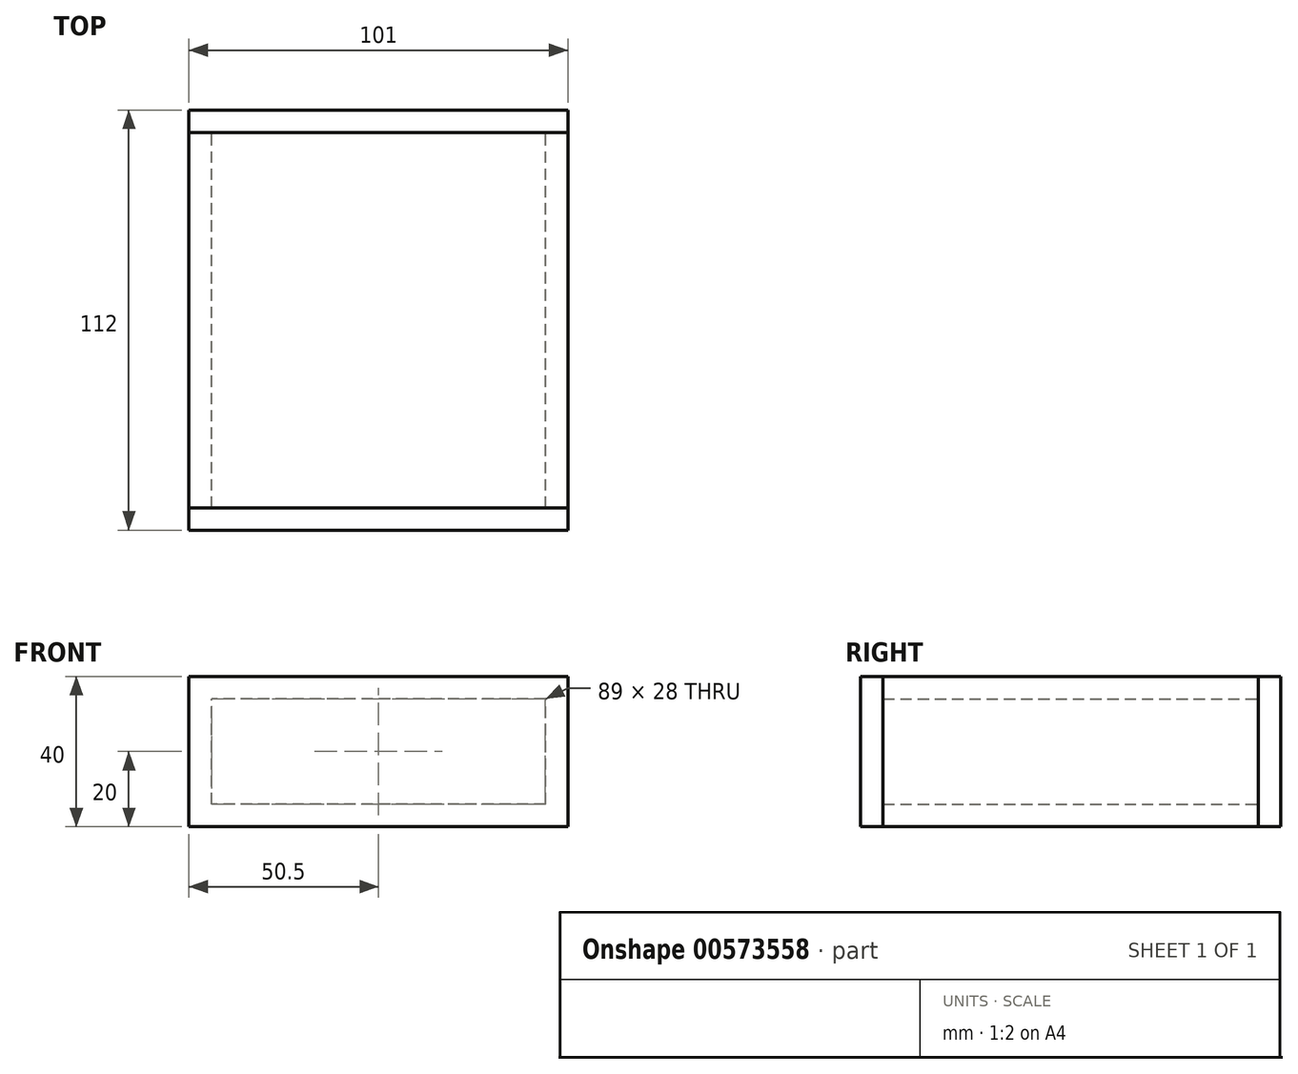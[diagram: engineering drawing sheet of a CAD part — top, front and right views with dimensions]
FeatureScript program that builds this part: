
annotation { "Feature Type Name" : "Feature", "Feature Type Description" : "" }
export const myFeature = defineFeature(function(context is Context, id is Id, definition is map)
    precondition{}
    {
        {
            var Q0;
            Q0=qCreatedBy(makeId("Front.planeOp"),FACE);
            var sketch = newSketch(context, id + "F0", { "sketchPlane" : qUnion([Q0])});
            skLineSegment(sketch, "E0.bottom", {"start": v(50.5, -20) * mm, "end": v(-50.5, -20) * mm});
            skLineSegment(sketch, "E0.top", {"start": v(50.5, 20) * mm, "end": v(-50.5, 20) * mm});
            skLineSegment(sketch, "E0.left", {"start": v(50.5, -20) * mm, "end": v(50.5, 20) * mm});
            skLineSegment(sketch, "E0.right", {"start": v(-50.5, -20) * mm, "end": v(-50.5, 20) * mm});
            skPoint(sketch, "E0.middle", {"position": v(0, 0) * mm});
            skSolve(sketch);
        }
        {
            var Q0;
            Q0=makeQuery(id+"F0.imprint","IMPRINT",FACE,{"disambiguationData":[TD([[makeQuery(id+"F0.imprint","IMPRINT",EDGE,{"derivedFrom":sQuery(id+"F0.wireOp",EDGE,"E0.bottom")}),-1.0]])]});
            extrude(context, id + "F1", {"entities" : qUnion([Q0]), "depth" : 6 * mm, "offsetDistance" : 25 * mm});
        }
        {
            var Q0;
            Q0=makeQuery(id+"F1.opExtrude","CAP_FACE",FACE,{"disambiguationData":[OSD([sQuery(id+"F0.wireOp",EDGE,"E0.bottom"),sQuery(id+"F0.wireOp",EDGE,"E0.top"),sQuery(id+"F0.wireOp",EDGE,"E0.left"),sQuery(id+"F0.wireOp",EDGE,"E0.right")])],"isStart":false});
            var sketch = newSketch(context, id + "F2", { "sketchPlane" : qUnion([Q0])});
            skLineSegment(sketch, "E1.0", {"start": v(50.5, -20) * mm, "end": v(50.5, 20) * mm});
            skLineSegment(sketch, "E2.0", {"start": v(50.5, 20) * mm, "end": v(-50.5, 20) * mm});
            skLineSegment(sketch, "E3.0", {"start": v(50.5, -20) * mm, "end": v(-50.5, -20) * mm});
            skLineSegment(sketch, "E4.0", {"start": v(-50.5, -20) * mm, "end": v(-50.5, 20) * mm});
            skLineSegment(sketch, "E5.0", {"start": v(44.5, -14) * mm, "end": v(44.5, 14) * mm});
            skLineSegment(sketch, "E5.1", {"start": v(44.5, -14) * mm, "end": v(-44.5, -14) * mm});
            skLineSegment(sketch, "E5.2", {"start": v(-44.5, -14) * mm, "end": v(-44.5, 14) * mm});
            skLineSegment(sketch, "E5.3", {"start": v(44.5, 14) * mm, "end": v(-44.5, 14) * mm});
            skSolve(sketch);
        }
        {
            var Q0;
            Q0 = qSketchRegion(id + "F2", true);
            extrude(context, id + "F3", {"entities" : qUnion([Q0]), "depth" : 100 * mm, "offsetDistance" : 25 * mm});
        }
        {
            var Q0;
            Q0=makeQuery(id+"F1.opExtrude","SWEPT_BODY",BODY,{"disambiguationData":[OSD([sQuery(id+"F0.wireOp",EDGE,"E0.bottom"),sQuery(id+"F0.wireOp",EDGE,"E0.top"),sQuery(id+"F0.wireOp",EDGE,"E0.left"),sQuery(id+"F0.wireOp",EDGE,"E0.right")])]});
            transform(context, id + "F4", {"entities" : qUnion([Q0]), "transformType" : TransformType.TRANSLATION_3D, "dx" : 0 * mm, "dy" : -106 * mm, "dz" : 0 * mm, "makeCopy" : true});
        }
    });
